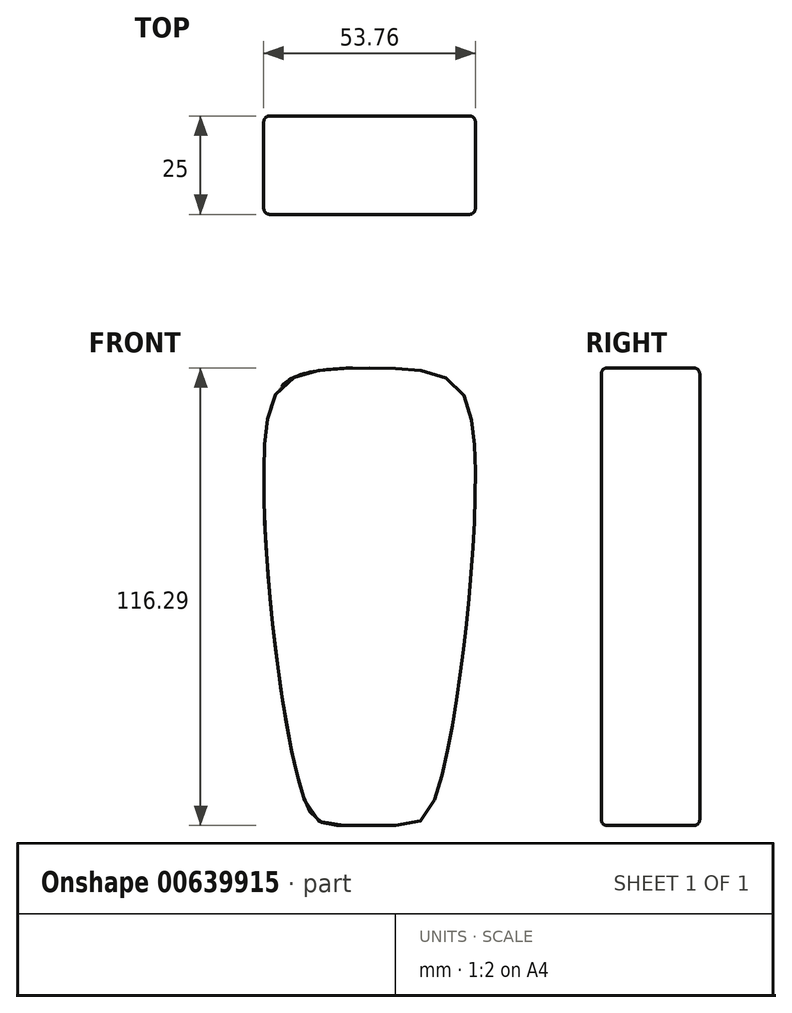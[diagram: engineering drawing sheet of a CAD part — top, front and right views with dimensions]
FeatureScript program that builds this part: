
annotation { "Feature Type Name" : "Feature", "Feature Type Description" : "" }
export const myFeature = defineFeature(function(context is Context, id is Id, definition is map)
    precondition{}
    {
        {
            var Q0;
            Q0=qCreatedBy(makeId("Front.planeOp"),FACE);
            var sketch = newSketch(context, id + "F0", { "sketchPlane" : qUnion([Q0])});
            skFitSpline(sketch, "E0", {"points": [v(0, 61.42) * mm, v(-26.34, 45.27) * mm, v(-16.24, -49.06) * mm, v(0, -54.84) * mm], "startDerivative": vector(-215.98, 0) * mm, "endDerivative": vector(157.36, 0) * mm});
            skFitSpline(sketch, "E1.MirrorCS", {"points": [v(0, 61.42) * mm, v(26.34, 45.27) * mm, v(16.24, -49.06) * mm, v(0, -54.84) * mm], "startDerivative": vector(215.98, 0) * mm, "endDerivative": vector(-157.36, 0) * mm});
            skPoint(sketch, "E2", {"position": v(-25, 0) * mm});
            skPoint(sketch, "E3", {"position": v(25, 0) * mm});
            skLineSegment(sketch, "E4", {"start": v(-25, 0) * mm, "end": v(25, 0) * mm, "construction": true});
            skLineSegment(sketch, "E5", {"start": v(-20.57, 61.42) * mm, "end": v(20.57, 61.42) * mm, "construction": true});
            skLineSegment(sketch, "E6", {"start": v(11.2, -54.84) * mm, "end": v(-11.2, -54.84) * mm, "construction": true});
            skSolve(sketch);
        }
        {
            var Q0;
            Q0=makeQuery(id+"F0.imprint","IMPRINT",FACE,{"disambiguationData":[TD([[makeQuery(id+"F0.imprint","IMPRINT",EDGE,{"derivedFrom":sQuery(id+"F0.wireOp",EDGE,"E0")}),1.0]])]});
            extrude(context, id + "F1", {"entities" : qUnion([Q0]), "depth" : 25 * mm, "offsetDistance" : 25 * mm});
        }
        {
            var Q0;
            Q0=makeQuery(id+"F1.opExtrude","CAP_EDGE",EDGE,{"disambiguationData":[OSD([sQuery(id+"F0.wireOp",EDGE,"E0")])],"isStart":false});
            var Q1;
            Q1=makeQuery(id+"F1.opExtrude","CAP_FACE",FACE,{"disambiguationData":[OSD([sQuery(id+"F0.wireOp",EDGE,"E0"),sQuery(id+"F0.wireOp",EDGE,"E1.MirrorCS")])],"isStart":false});
            var Q2;
            Q2=makeQuery(id+"F1.opExtrude","CAP_EDGE",EDGE,{"disambiguationData":[OSD([sQuery(id+"F0.wireOp",EDGE,"E0")])],"isStart":true});
            var Q3;
            Q3=makeQuery(id+"F1.opExtrude","CAP_EDGE",EDGE,{"disambiguationData":[OSD([sQuery(id+"F0.wireOp",EDGE,"E1.MirrorCS")])],"isStart":true});
            fillet(context, id + "F2", {"entities" : qUnion([Q0, Q1, Q2, Q3]), "radius" : 1.5 * mm, "tangentPropagation" : true, "defaultsChanged" : true, "vertexSettings" : [], "allowEdgeOverflow" : false});
        }
    });
